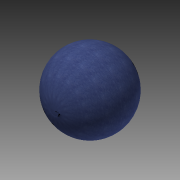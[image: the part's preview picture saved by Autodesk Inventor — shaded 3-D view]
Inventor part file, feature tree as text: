
AUTODESK INVENTOR PART (.ipt)
format: ipt  version: 2013 (Build 170138000, 138)  size: 115,200 bytes
history: native  units: in
note: dims shown in document units (in); Inventor stores cm internally (conversion verified against a paired STEP export)
features: revolve x1, sketch x1
ambient origin geometry x8: Origin, YZ Plane, XZ Plane, XY Plane, X Axis, Y Axis, Z Axis, Center Point
bodies: Solid1 (feature_tree)
feature tree (2):
  revolve  "Revolution1"  Angle=90.0deg
  sketch  "Sketch1"  dims[d0=24.0in d1=90.0deg]
